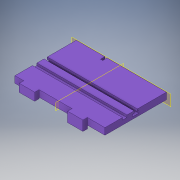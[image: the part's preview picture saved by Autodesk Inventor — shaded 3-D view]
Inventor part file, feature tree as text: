
AUTODESK INVENTOR PART (.ipt)
format: ipt  version: 2018.2 (Build 222227000, 227)  size: 208,896 bytes
history: native  units: in
note: dims shown in document units (in); Inventor stores cm internally (conversion verified against a paired STEP export)
features: extrude x6, sketch x5, mirror x4, split x1, plane x1
ambient origin geometry x8: Origin, YZ Plane, XZ Plane, XY Plane, X Axis, Y Axis, Z Axis, Center Point
bodies: Solid1 (feature_tree)
feature tree (17):
  extrude  "Extrusion1"  Depth=0.375in
  extrude  "Extrusion2"  Depth=0.75in
  mirror  "Mirror1"
  extrude  "Extrusion3"  Depth=7.0in TaperAngle=0.0deg
  extrude  "Extrusion4"  Depth=0.5in TaperAngle=0.0deg
  mirror  "Mirror2"
  extrude  "Extrusion5"  Depth=0.25in
  mirror  "Mirror3"
  extrude  "Extrusion8"  Depth=3.5in
  mirror  "Mirror4"
  split  "Split2"
  plane  "Work Plane1"
  sketch  "Sketch4"  dims[d0=0.375in d1=0.375in]
  sketch  "Sketch6"  dims[d6=2.5in d8=0.75in]
  sketch  "Sketch7"  dims[d9=7.0in d10=14.0in d11=0.0in]
  sketch  "Sketch9"  dims[d12=0.875in d13=0.5in d14=0.0in]
  sketch  "Sketch12"  dims[d16=0.5in d18=0.25in d19=3.5in d20=1.0in d21=0.0in d22=1.75in d23=0.9in d24=1.0in d25=0.5in d26=0.0in d28=0.5in d29=0.25in d30=2.0in d31=0.5in d32=0.0in d46=3.5in d47=0.1875in d48=0.25in d49=0.25in d50=0.344in d51=0.5in d52=0.0in d53=-5.25in]
